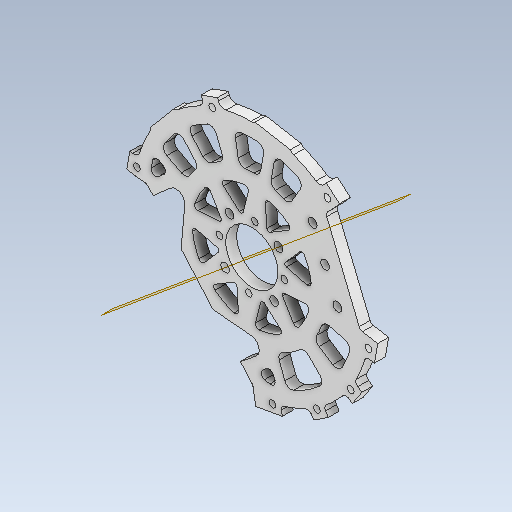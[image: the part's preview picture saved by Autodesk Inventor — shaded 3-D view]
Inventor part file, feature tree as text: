
AUTODESK INVENTOR PART (.ipt)
format: ipt  version: 2020 (Build 240168000, 168)  size: 1,191,936 bytes
history: native  units: mm
features: reference x14, sketch x11, extrude x10, projected_geometry x6, fillet x4, other x4, mirror x2, shell x2, hole x1, thicken_offset x1, pattern_circular x1, plane x1
ambient origin geometry x8: Origin, YZ Plane, XZ Plane, XY Plane, X Axis, Y Axis, Z Axis, Center Point
bodies: Solid1 (feature_tree)
feature tree (57):
  extrude  "Extrusion1"  Depth=5.0mm TaperAngle=0.0deg
  hole  "Hole1"  [1 undecoded]
  extrude  "Extrusion2"  Depth=5.0mm
  extrude  "Extrusion3"  Depth=4.0mm
  thicken_offset  "Thicken1"
  pattern_circular  "Circular Pattern1"  Count=8 Angle=360.0deg
  extrude  "Extrusion4"  Depth=8.0mm
  plane  "Work Plane1"
  mirror  "Mirror1"
  extrude  "Extrusion5"  Depth=5.0mm TaperAngle=0.0deg
  mirror  "Mirror2"
  extrude  "Extrusion6"  Depth=95.0mm
  extrude  "Extrusion7"  Depth=4.363323mm
  extrude  "Extrusion8"  Depth=4.363323mm
  extrude  "Extrusion9"  Depth=5.0mm
  fillet  "Fillet1"  Radius=2.094395mm
  fillet  "Fillet2"  Radius=6.981317mm
  fillet  "Fillet3"  Radius=1.745329mm
  fillet  "Fillet4"  Radius=5.0mm
  extrude  "Extrusion10"  Depth=5.0mm
  sketch  "Sketch1"  dims[d0=60.0mm d1=5.0mm d2=0.0mm]
  reference  "Reference1"
  reference  "Reference2"
  reference  "Reference3"
  sketch  "Sketch2"  dims[d3=3.1mm d4=6.0mm d5=4.0mm d6=2.0mm d7=90.0deg d8=17.0mm d9=0.0mm d10=60.0mm]
  reference  "Reference4"
  reference  "Reference5"
  reference  "Reference6"
  reference  "Reference7"
  reference  "Reference8"
  reference  "Reference9"
  reference  "Reference10"
  sketch  "Sketch3"  dims[d11=5.0mm d12=0.0mm d13=60.0mm]
  sketch  "Sketch5"  dims[d21=15.0mm d22=8.0mm]
  reference  "Reference11"
  reference  "Reference12"
  reference  "Reference13"
  reference  "Reference14"
  sketch  "Sketch6"  dims[d23=5.0mm d24=0.0mm d25=5.0mm d26=0.0mm]
  projected_geometry  "Projected Loop1"
  sketch  "Sketch7"  dims[d27=68.0mm d28=95.0mm]
  projected_geometry  "Projected Loop2"
  sketch  "Sketch8"  dims[d29=1.745329mm d30=4.363323mm]
  projected_geometry  "Projected Loop3"
  sketch  "Sketch9"  dims[d31=2.094395mm d32=4.363323mm]
  projected_geometry  "Projected Loop4"
  sketch  "Sketch10"  dims[d33=1.745329mm d34=6.981317mm d35=2.094395mm d36=6.981317mm d37=1.745329mm d39=5.0mm d40=0.0mm]
  projected_geometry  "Projected Loop5"
  sketch  "Sketch11"  dims[d41=5.0mm d42=5.0mm d43=5.0mm d44=0.0mm d45=0.872665mm d46=5.0mm d47=0.0mm d48=5.0mm d49=5.0mm d50=10.0mm d51=5.0mm d52=5.0mm d53=10.0mm d54=5.0mm d55=0.0mm d56=3.0mm d57=3.0mm d58=2.0mm d59=2.0mm d60=3.0mm d61=15.0mm d62=4.1mm d63=4.1mm d64=15.0mm d65=4.1mm d66=10.0mm d67=0.0mm]
  projected_geometry  "Projected Loop6"
  parser-record x1  (decoder bookkeeping rows leaked as tree rows — omitted from the tree; the rows remain in map.json)
  other  "reducer_2.iam"
  other  "90_motor:1"
  other  "90motor_base:1"
  shell  "shell_5:1"  Thickness=5.0mm
  shell  "shell_3:1"  Thickness=0.872665mm
  sketch  "Sketch4"  dims[d14=5.0mm d15=0.0mm d16=4.0mm d17=1.0mm d18=80.0mm d19=360.0deg]
note: 1 required parameter value undecoded (feature->parameter linkage not recoverable at this tier; creation-order binding heuristic only, values carry confidence <= 0.55)
note: 1 file-system path scrubbed to <path> (originals preserved in map.json)
